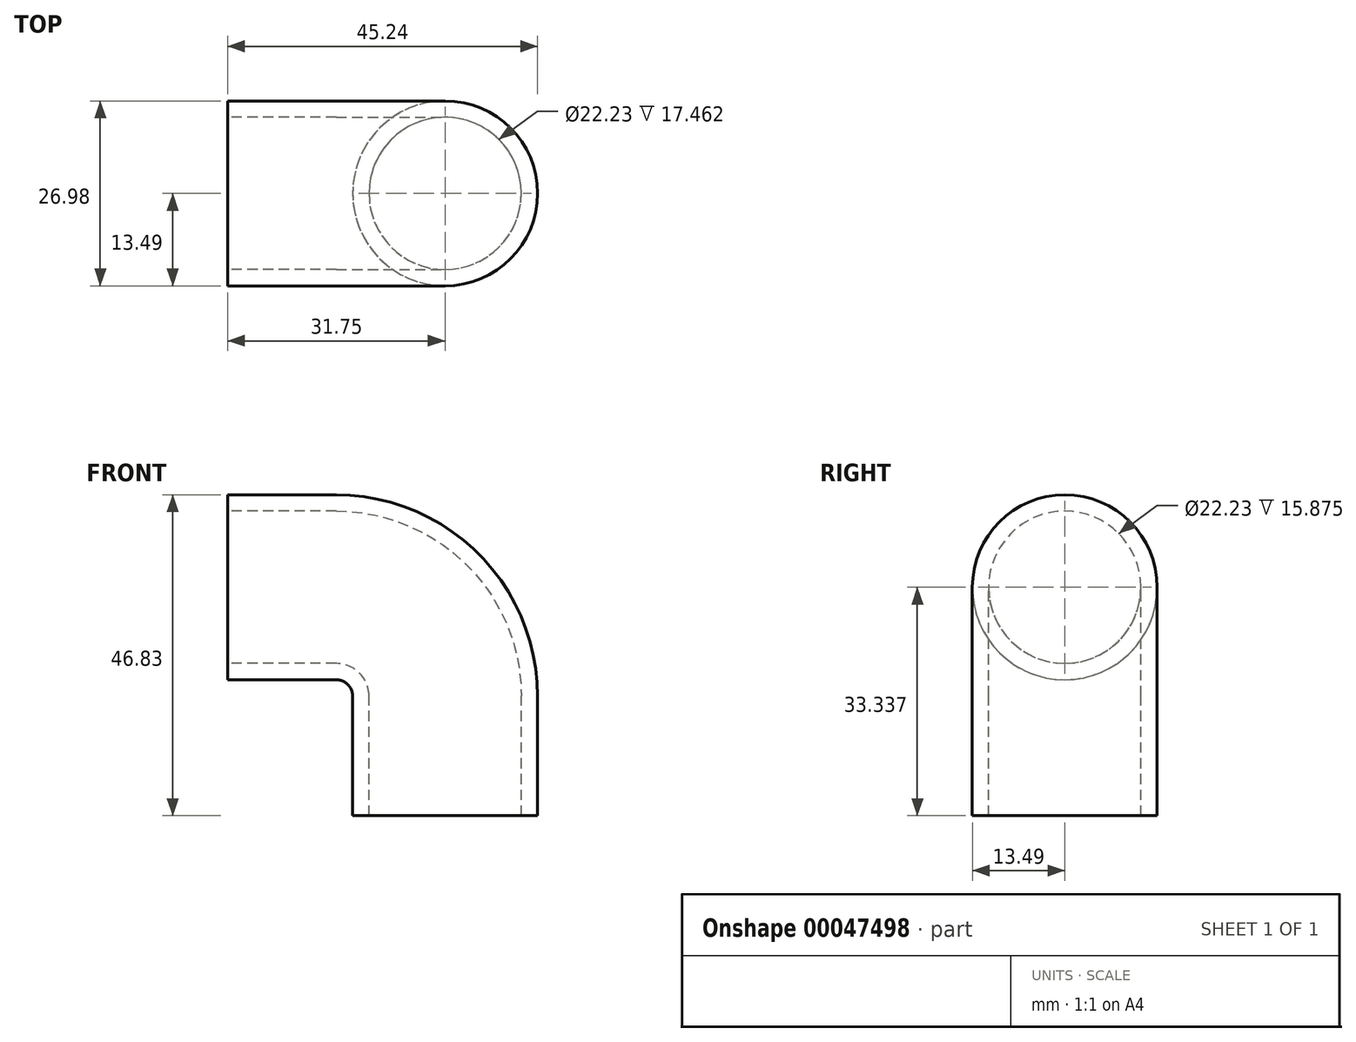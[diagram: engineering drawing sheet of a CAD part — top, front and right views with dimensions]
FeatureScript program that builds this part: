
annotation { "Feature Type Name" : "Feature", "Feature Type Description" : "" }
export const myFeature = defineFeature(function(context is Context, id is Id, definition is map)
    precondition{}
    {
        {
            var Q0;
            Q0=qCreatedBy(makeId("Front.planeOp"),FACE);
            var sketch = newSketch(context, id + "F0", { "sketchPlane" : qUnion([Q0])});
            skLineSegment(sketch, "E0", {"start": v(0, 0) * mm, "end": v(0, 17.46) * mm});
            skLineSegment(sketch, "E1", {"start": v(-15.88, 33.34) * mm, "end": v(-31.75, 33.34) * mm});
            skPoint(sketch, "E2.visualSharp", {"position": v(0, 33.34) * mm});
            skArc(sketch, "E2.filletArc", {"start": v(0, 17.46) * mm, "mid": v(-4.65, 28.69) * mm, "end": v(-15.88, 33.34) * mm});
            skSolve(sketch);
        }
        {
            var Q0;
            Q0=qCreatedBy(makeId("Top.planeOp"),FACE);
            var sketch = newSketch(context, id + "F1", { "sketchPlane" : qUnion([Q0])});
            skCircle(sketch, "E3", {"center": v(0, 0) * mm, "radius": 13.5 * mm});
            skSolve(sketch);
        }
        {
            var Q0;
            Q0 = qSketchRegion(id + "F1", true);
            var Q1;
            Q1 = qConstructionFilter(qBodyType(qCreatedBy(id + "F0" ,EDGE), BodyType.WIRE), ConstructionObject.NO);
            sweep(context, id + "F2", {"profiles" : qUnion([Q0]), "path" : qUnion([Q1])});
        }
        {
            var Q0;
            Q0=makeQuery(id+"F2.opSweep","CAP_FACE",FACE,{"disambiguationData":[OSD([sQuery(id+"F0.wireOp",VERTEX,"E0.start"),sQuery(id+"F1.wireOp",EDGE,"E3")])],"isStart":true});
            var sketch = newSketch(context, id + "F3", { "sketchPlane" : qUnion([Q0])});
            skCircle(sketch, "E4", {"center": v(0, 0) * mm, "radius": 11.11 * mm});
            skSolve(sketch);
        }
        {
            var Q0;
            Q0=makeQuery(id+"F3.imprint","IMPRINT",FACE,{"disambiguationData":[TD([[makeQuery(id+"F3.imprint","IMPRINT",EDGE,{"derivedFrom":sQuery(id+"F3.wireOp",EDGE,"E4")}),1.0]])]});
            var Q1;
            Q1 = qConstructionFilter(qBodyType(qCreatedBy(id + "F0" ,EDGE), BodyType.WIRE), ConstructionObject.NO);
            sweep(context, id + "F4", {"operationType" : NewBodyOperationType.REMOVE, "profiles" : qUnion([Q0]), "path" : qUnion([Q1])});
        }
    });
